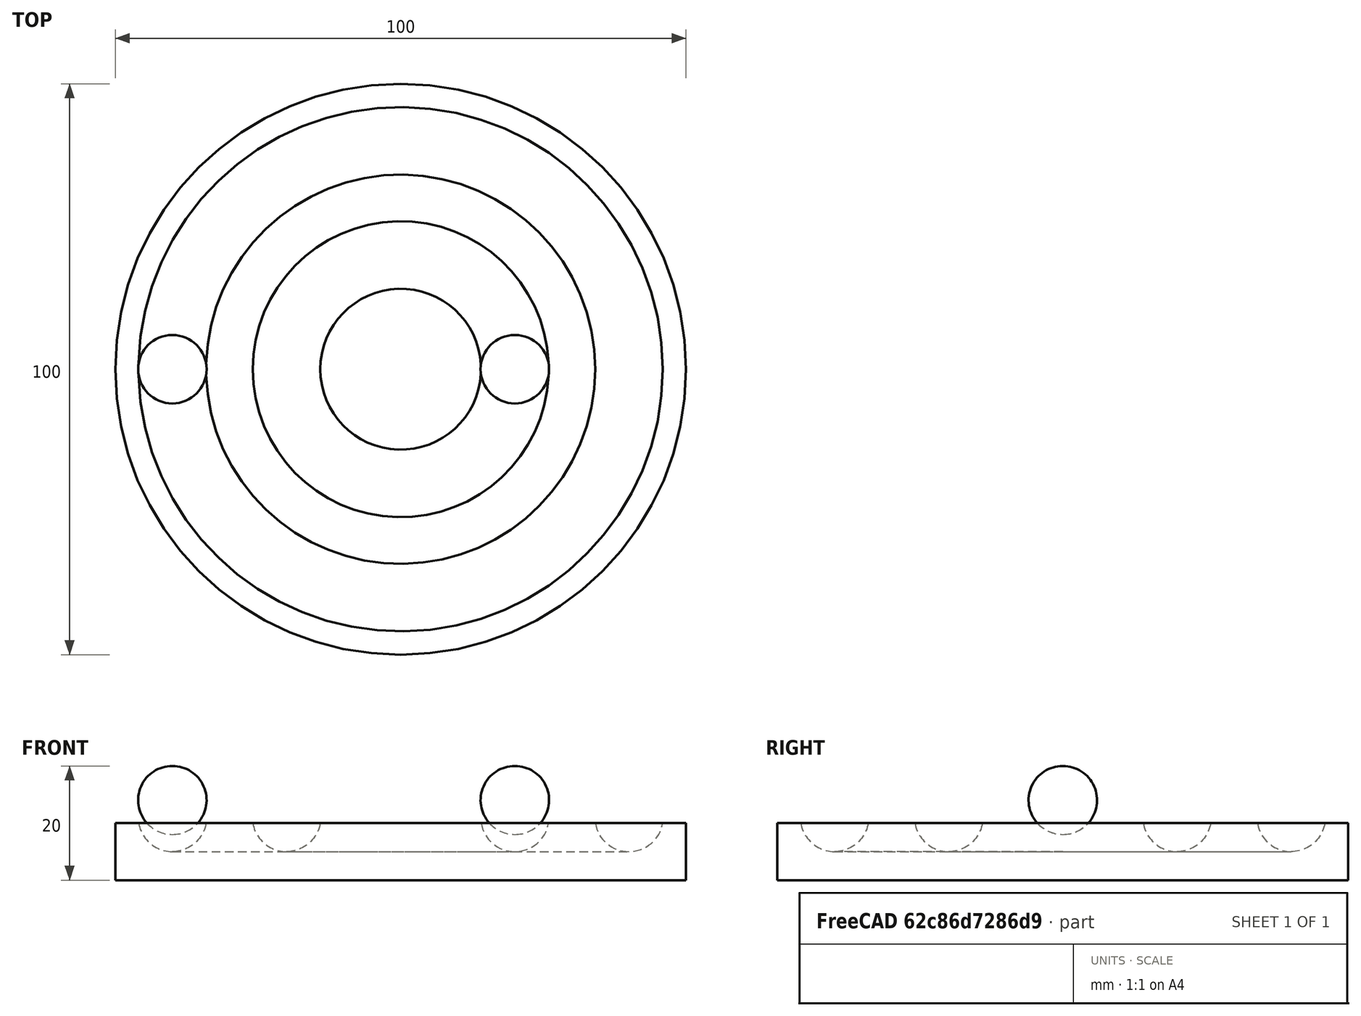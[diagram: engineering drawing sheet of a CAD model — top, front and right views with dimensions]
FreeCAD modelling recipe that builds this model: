
FCSTD DOCUMENT  (FreeCAD 0.21R33694 (Git))
Label: OJT1_T15R01_canicas
License: All rights reserved
LicenseURL: http://en.wikipedia.org/wiki/All_rights_reserved
objects: Part::Torus×2, Part::Cut×2, Part::Sphere×2, Part::Cylinder×1
note: 7 computed .brp shape members not serialized (recipe doc carries the construction recipe); baked Part::Feature solids carry a one-line shape summary decoded from their .brp

FEATURE [Part::Cylinder] Cylinder
  Angle = 360
  AttacherType = Attacher::AttachEngine3D
  FirstAngle = 0
  Height = 10
  Radius = 50
  SecondAngle = 0
FEATURE [Part::Torus] Torus
  Angle1 = -180
  Angle2 = 180
  Angle3 = 360
  AttacherType = Attacher::AttachEngine3D
  Placement = pos=(0,0,11) rot=(0,0,1;0rad)
  Radius1 = 40
  Radius2 = 6
FEATURE [Part::Torus] Torus001
  Angle1 = -180
  Angle2 = 180
  Angle3 = 360
  AttacherType = Attacher::AttachEngine3D
  Placement = pos=(0,0,11) rot=(0,0,1;0rad)
  Radius1 = 20
  Radius2 = 6
FEATURE [Part::Cut] Cut
  Base = -> Cylinder
  Refine = true
  Tool = -> Torus
FEATURE [Part::Cut] Cut001
  Base = -> Cut
  Refine = true
  Tool = -> Torus001
FEATURE [Part::Sphere] Sphere
  Angle1 = -90
  Angle2 = 90
  Angle3 = 360
  AttacherType = Attacher::AttachEngine3D
  Placement = pos=(20,0,14) rot=(0,0,1;0rad)
  Radius = 6
FEATURE [Part::Sphere] Sphere001
  Angle1 = -90
  Angle2 = 90
  Angle3 = 360
  AttacherType = Attacher::AttachEngine3D
  Placement = pos=(-40,0,14) rot=(0,0,1;0rad)
  Radius = 6
